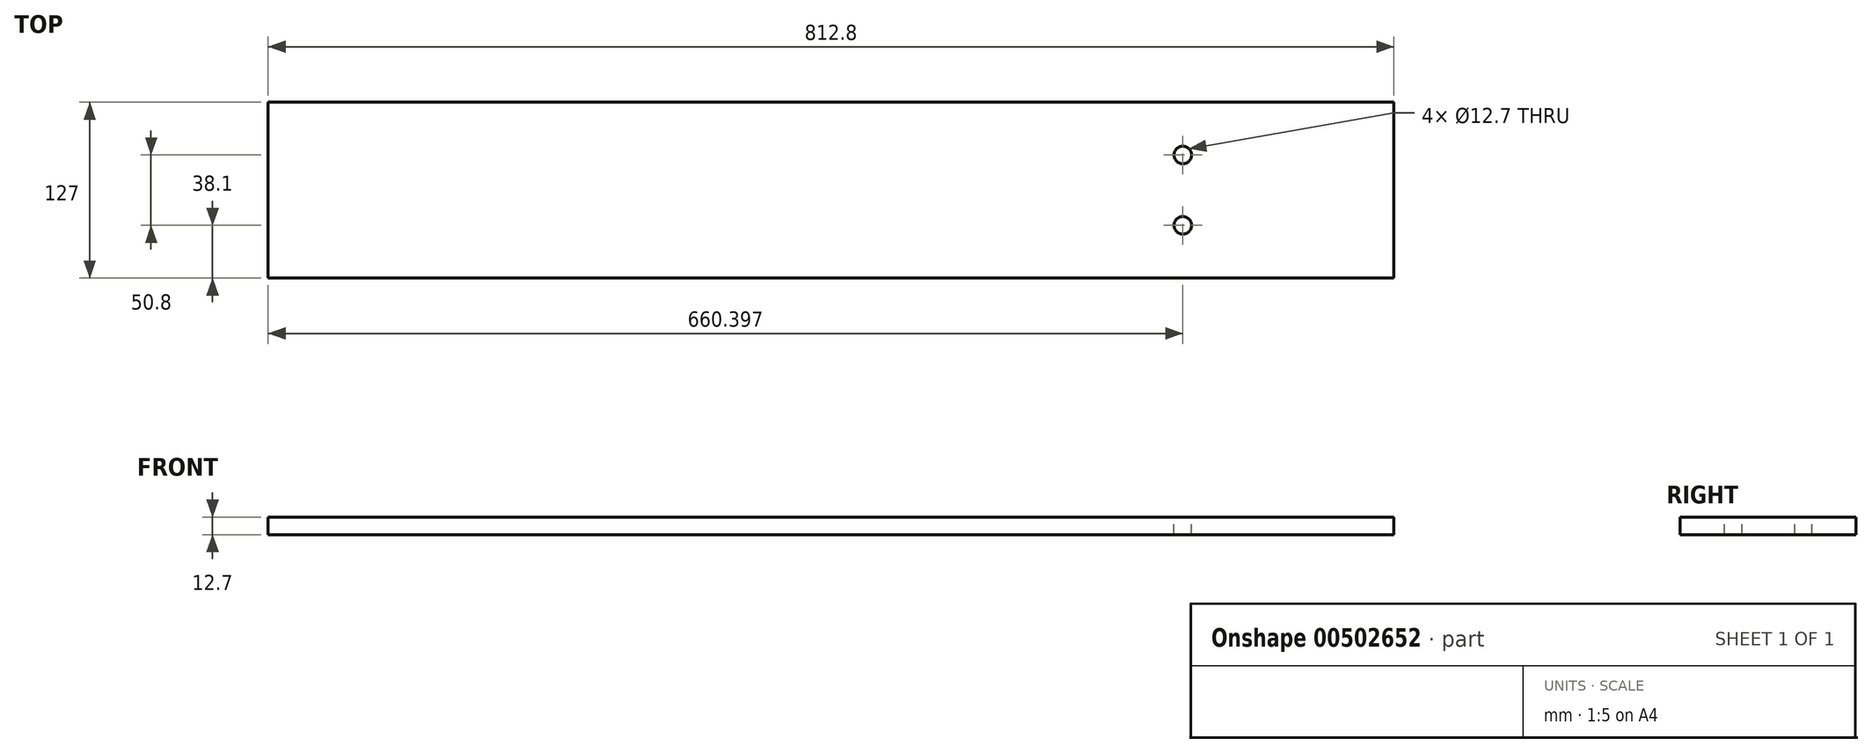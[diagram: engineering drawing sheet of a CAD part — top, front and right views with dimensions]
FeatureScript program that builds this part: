
annotation { "Feature Type Name" : "Feature", "Feature Type Description" : "" }
export const myFeature = defineFeature(function(context is Context, id is Id, definition is map)
    precondition{}
    {
        {
            var Q0;
            Q0=qCreatedBy(makeId("Front.planeOp"),FACE);
            var sketch = newSketch(context, id + "F0", { "sketchPlane" : qUnion([Q0])});
            skLineSegment(sketch, "E0.bottom", {"start": v(-280.6, 7.3) * mm, "end": v(532.2, 7.3) * mm});
            skLineSegment(sketch, "E0.top", {"start": v(-280.6, -5.4) * mm, "end": v(532.2, -5.4) * mm});
            skLineSegment(sketch, "E0.left", {"start": v(-280.6, 7.3) * mm, "end": v(-280.6, -5.4) * mm});
            skLineSegment(sketch, "E0.right", {"start": v(532.2, 7.3) * mm, "end": v(532.2, -5.4) * mm});
            skSolve(sketch);
        }
        {
            var Q0;
            Q0=makeQuery(id+"F0.imprint","IMPRINT",FACE,{"disambiguationData":[TD([[makeQuery(id+"F0.imprint","IMPRINT",EDGE,{"derivedFrom":sQuery(id+"F0.wireOp",EDGE,"E0.bottom")}),-1.0]])]});
            extrude(context, id + "F1", {"entities" : qUnion([Q0]), "depth" : 127 * mm});
        }
        {
            var Q0;
            Q0=makeQuery(id+"F1.opExtrude","SWEPT_FACE",FACE,{"disambiguationData":[OSD([sQuery(id+"F0.wireOp",EDGE,"E0.bottom")])]});
            var sketch = newSketch(context, id + "F2", { "sketchPlane" : qUnion([Q0])});
            skCircle(sketch, "E1", {"center": v(379.8, -38.1) * mm, "radius": 6.35 * mm});
            skCircle(sketch, "E2", {"center": v(379.8, -88.9) * mm, "radius": 6.35 * mm});
            skSolve(sketch);
        }
        {
            var Q0;
            Q0=makeQuery(id+"F2.imprint","IMPRINT",FACE,{"disambiguationData":[TD([[makeQuery(id+"F2.imprint","IMPRINT",EDGE,{"derivedFrom":sQuery(id+"F2.wireOp",EDGE,"E1")}),1.0]])]});
            var Q1;
            Q1=makeQuery(id+"F2.imprint","IMPRINT",FACE,{"disambiguationData":[TD([[makeQuery(id+"F2.imprint","IMPRINT",EDGE,{"derivedFrom":sQuery(id+"F2.wireOp",EDGE,"E2")}),1.0]])]});
            extrude(context, id + "F3", {"entities" : qUnion([Q0, Q1]), "operationType" : NewBodyOperationType.REMOVE, "endBound" : BoundingType.THROUGH_ALL, "oppositeDirection" : true, "depth" : 25.4 * mm});
        }
    });
